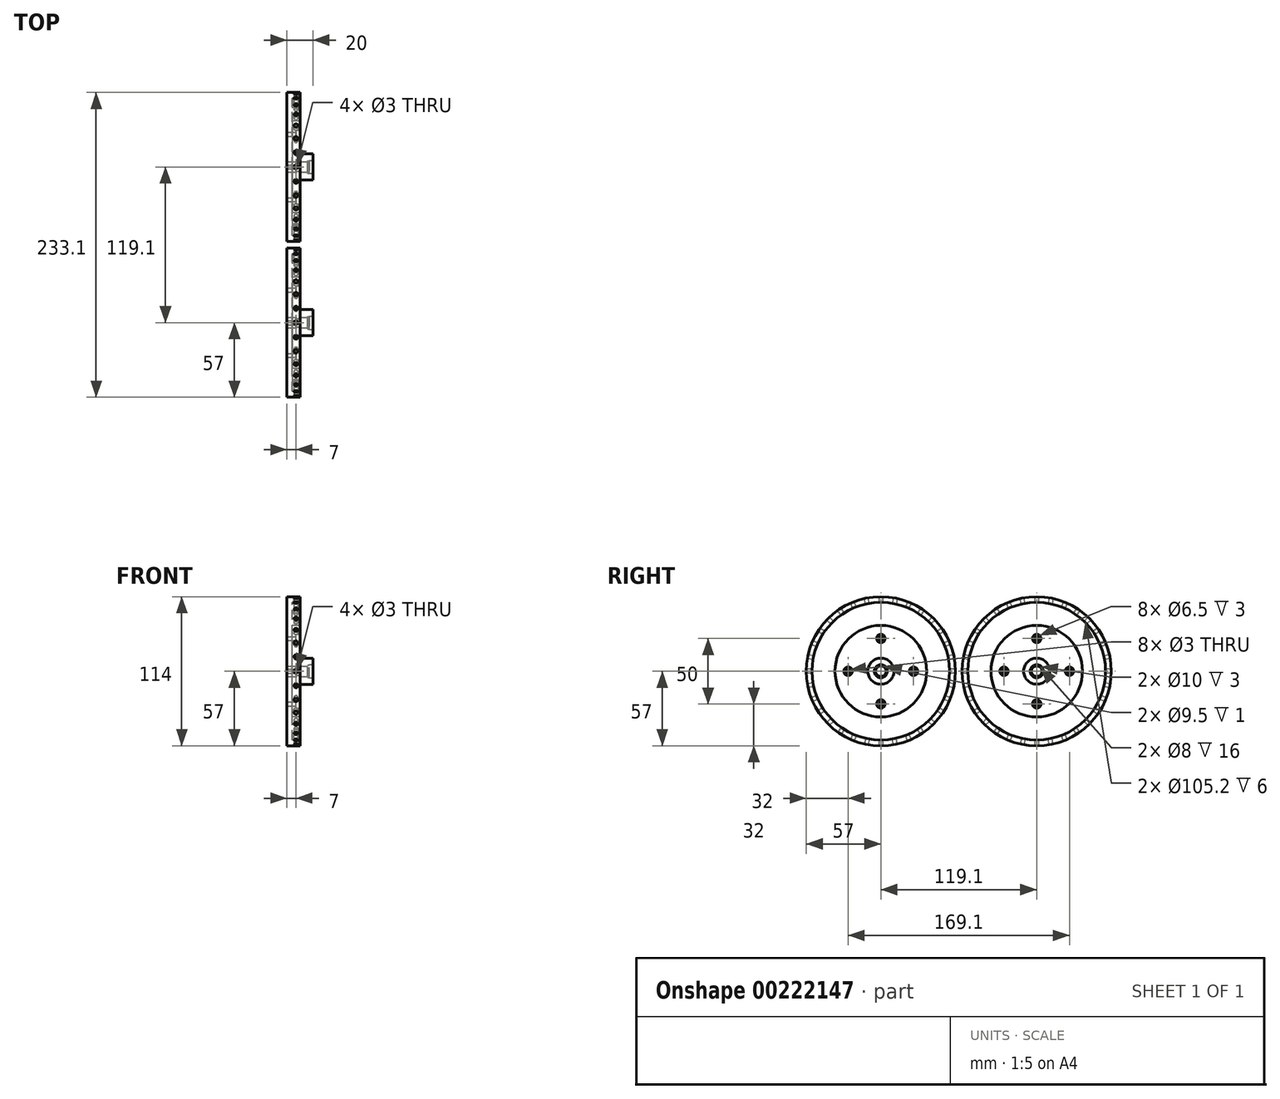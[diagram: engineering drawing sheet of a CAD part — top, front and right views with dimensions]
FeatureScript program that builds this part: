
annotation { "Feature Type Name" : "Feature", "Feature Type Description" : "" }
export const myFeature = defineFeature(function(context is Context, id is Id, definition is map)
    precondition{}
    {
        {
            var Q0;
            Q0=qCreatedBy(makeId("Right.planeOp"),FACE);
            var sketch = newSketch(context, id + "F0", { "sketchPlane" : qUnion([Q0])});
            skCircle(sketch, "E0", {"center": v(0, 0) * mm, "radius": 57 * mm});
            skCircle(sketch, "E1", {"center": v(0, 0) * mm, "radius": 52.6 * mm});
            skSolve(sketch);
        }
        {
            var Q0;
            Q0=qSketchRegion(id+"F0",true);
            extrude(context, id + "F1", {"entities" : qUnion([Q0]), "endBound" : BoundingType.SYMMETRIC, "depth" : 20 * mm});
        }
        {
            var Q0;
            Q0=qCreatedBy(makeId("Right.planeOp"),FACE);
            var sketch = newSketch(context, id + "F2", { "sketchPlane" : qUnion([Q0])});
            skCircle(sketch, "E2", {"center": v(0, 0) * mm, "radius": 52.6 * mm});
            skCircle(sketch, "E3", {"center": v(0, 0) * mm, "radius": 4 * mm});
            skSolve(sketch);
        }
        {
            var Q0;
            Q0=qSketchRegion(id+"F2",true);
            extrude(context, id + "F3", {"entities" : qUnion([Q0]), "operationType" : NewBodyOperationType.ADD, "endBound" : BoundingType.SYMMETRIC, "depth" : 8 * mm});
        }
        {
            var Q0;
            Q0=qCreatedBy(makeId("Top.planeOp"),FACE);
            var sketch = newSketch(context, id + "F4", { "sketchPlane" : qUnion([Q0])});
            skCircle(sketch, "E4", {"center": v(0, 0) * mm, "radius": 7 * mm, "construction": true});
            skCircle(sketch, "E5", {"center": v(-7, 0) * mm, "radius": 1.5 * mm});
            skCircle(sketch, "E6", {"center": v(7, 0) * mm, "radius": 1.5 * mm});
            skSolve(sketch);
        }
        {
            var Q0;
            Q0=qSketchRegion(id+"F4",true);
            extrude(context, id + "F5", {"entities" : qUnion([Q0]), "endBound" : BoundingType.SYMMETRIC, "depth" : 160 * mm, "hasSecondDirection" : true, "secondDirectionBound" : SecondDirectionBoundingType.THROUGH_ALL, "secondDirectionOppositeDirection" : true, "secondDirectionDepth" : 25 * mm});
        }
        {
            var Q0;
            Q0=qCreatedBy(makeId("Front.planeOp"),FACE);
            var sketch = newSketch(context, id + "F6", { "sketchPlane" : qUnion([Q0])});
            skLineSegment(sketch, "E7", {"start": v(28.93, 0) * mm, "end": v(-37.29, 0) * mm, "construction": true});
            skSolve(sketch);
        }
        {
            var Q0;
            Q0=makeQuery(id+"F5.opExtrude","SWEPT_BODY",BODY,{"disambiguationData":[OSD([sQuery(id+"F4.wireOp",EDGE,"E6")])]});
            var Q1;
            Q1=makeQuery(id+"F5.opExtrude","SWEPT_BODY",BODY,{"disambiguationData":[OSD([sQuery(id+"F4.wireOp",EDGE,"E5")])]});
            var Q2;
            Q2=sQuery(id+"F6.wireOp",EDGE,"E7");
            circularPattern(context, id + "F7", {"operationType" : NewBodyOperationType.REMOVE, "entities" : qUnion([Q0, Q1]), "axis" : qUnion([Q2]), "angle" : 180 * degree, "instanceCount" : 17, "equalSpace" : true});
        }
        {
            var Q0;
            Q0=qCreatedBy(makeId("Right.planeOp"),FACE);
            var sketch = newSketch(context, id + "F8", { "sketchPlane" : qUnion([Q0])});
            skCircle(sketch, "E8", {"center": v(0, 0) * mm, "radius": 10 * mm});
            skSolve(sketch);
        }
        {
            var Q0;
            Q0=qSketchRegion(id+"F8",true);
            extrude(context, id + "F9", {"entities" : qUnion([Q0]), "operationType" : NewBodyOperationType.ADD, "endBound" : BoundingType.SYMMETRIC, "depth" : 40 * mm});
        }
        {
            var Q0;
            Q0=makeQuery(id+"F9.opExtrude","CAP_FACE",FACE,{"disambiguationData":[OSD([sQuery(id+"F8.wireOp",EDGE,"E8")])],"isStart":false});
            var sketch = newSketch(context, id + "F10", { "sketchPlane" : qUnion([Q0])});
            skCircle(sketch, "E9", {"center": v(0, 0) * mm, "radius": 5 * mm});
            skSolve(sketch);
        }
        {
            var Q0;
            Q0=qSketchRegion(id+"F10",true);
            extrude(context, id + "F11", {"entities" : qUnion([Q0]), "operationType" : NewBodyOperationType.REMOVE, "oppositeDirection" : true, "depth" : 3 * mm});
        }
        {
            var Q0;
            Q0=makeQuery(id+"F9.opExtrude","CAP_FACE",FACE,{"disambiguationData":[OSD([sQuery(id+"F8.wireOp",EDGE,"E8")])],"isStart":true});
            var sketch = newSketch(context, id + "F12", { "sketchPlane" : qUnion([Q0])});
            skCircle(sketch, "E10", {"center": v(0, 0) * mm, "radius": 5 * mm});
            skSolve(sketch);
        }
        {
            var Q0;
            Q0=qSketchRegion(id+"F12",true);
            extrude(context, id + "F13", {"entities" : qUnion([Q0]), "operationType" : NewBodyOperationType.REMOVE, "oppositeDirection" : true, "depth" : 3 * mm});
        }
        {
            var Q0;
            Q0=makeQuery(id+"F11.boolean.opBoolean","COPY",FACE,{"derivedFrom":makeQuery(id+"F11.opExtrude","CAP_FACE",FACE,{"disambiguationData":[OSD([sQuery(id+"F10.wireOp",EDGE,"E9")])],"isStart":false})});
            var sketch = newSketch(context, id + "F14", { "sketchPlane" : qUnion([Q0])});
            skCircle(sketch, "E11", {"center": v(0, 0) * mm, "radius": 4.75 * mm});
            skSolve(sketch);
        }
        {
            var Q0;
            Q0=qSketchRegion(id+"F14",true);
            extrude(context, id + "F15", {"entities" : qUnion([Q0]), "operationType" : NewBodyOperationType.REMOVE, "oppositeDirection" : true, "depth" : 1 * mm});
        }
        {
            var Q0;
            Q0=makeQuery(id+"F13.boolean.opBoolean","COPY",FACE,{"derivedFrom":makeQuery(id+"F13.opExtrude","CAP_FACE",FACE,{"disambiguationData":[OSD([sQuery(id+"F12.wireOp",EDGE,"E10")])],"isStart":false})});
            var sketch = newSketch(context, id + "F16", { "sketchPlane" : qUnion([Q0])});
            skCircle(sketch, "E12", {"center": v(0, 0) * mm, "radius": 4.75 * mm});
            skSolve(sketch);
        }
        {
            var Q0;
            Q0=qSketchRegion(id+"F16",true);
            extrude(context, id + "F17", {"entities" : qUnion([Q0]), "operationType" : NewBodyOperationType.REMOVE, "oppositeDirection" : true, "depth" : 1 * mm});
        }
        {
            var Q0;
            Q0=makeQuery(id+"F9.opExtrude","CAP_FACE",FACE,{"disambiguationData":[OSD([sQuery(id+"F8.wireOp",EDGE,"E8")])],"isStart":false});
            var sketch = newSketch(context, id + "F18", { "sketchPlane" : qUnion([Q0])});
            skCircle(sketch, "E13", {"center": v(0, 0) * mm, "radius": 4 * mm});
            skSolve(sketch);
        }
        {
            var Q0;
            Q0=qSketchRegion(id+"F18",true);
            extrude(context, id + "F19", {"entities" : qUnion([Q0]), "operationType" : NewBodyOperationType.REMOVE, "endBound" : BoundingType.THROUGH_ALL, "oppositeDirection" : true, "depth" : 25 * mm});
        }
        {
            var Q0;
            Q0=qCreatedBy(makeId("Front.planeOp"),FACE);
            var sketch = newSketch(context, id + "F20", { "sketchPlane" : qUnion([Q0])});
            skCircle(sketch, "E14", {"center": v(0, 0) * mm, "radius": 17 * mm, "construction": true});
            skLineSegment(sketch, "E15", {"start": v(-17, 0) * mm, "end": v(-17, 16.39) * mm, "construction": true});
            skCircle(sketch, "E16", {"center": v(-17, 0) * mm, "radius": 10 * mm, "construction": true});
            skCircle(sketch, "E17", {"center": v(-17, 0) * mm, "radius": 8.5 * mm, "construction": true});
            skLineSegment(sketch, "E18", {"start": v(-17, 10) * mm, "end": v(-16, 10) * mm});
            skLineSegment(sketch, "E19", {"start": v(-16, 10) * mm, "end": v(-17, 8.5) * mm});
            skLineSegment(sketch, "E20.MirrorCS", {"start": v(-17, 10) * mm, "end": v(-18, 10) * mm});
            skLineSegment(sketch, "E21.MirrorCS", {"start": v(-18, 10) * mm, "end": v(-17, 8.5) * mm});
            skSolve(sketch);
        }
        {
            var Q0;
            Q0=qCreatedBy(makeId("Front.planeOp"),FACE);
            var sketch = newSketch(context, id + "F21", { "sketchPlane" : qUnion([Q0])});
            skLineSegment(sketch, "E22", {"start": v(-63.54, 0) * mm, "end": v(70.4, 0) * mm, "construction": true});
            skSolve(sketch);
        }
        {
            var Q0;
            Q0=qSketchRegion(id+"F20",true);
            var Q1;
            Q1=sQuery(id+"F21.wireOp",EDGE,"E22");
            revolve(context, id + "F22", {"operationType" : NewBodyOperationType.REMOVE, "entities" : qUnion([Q0]), "axis" : qUnion([Q1]), "revolveType" : RevolveType.FULL, "oppositeDirection" : true});
        }
        {
            var Q0;
            Q0=qCreatedBy(makeId("Right.planeOp"),FACE);
            var sketch = newSketch(context, id + "F23", { "sketchPlane" : qUnion([Q0])});
            skCircle(sketch, "E23", {"center": v(0, 0) * mm, "radius": 4 * mm});
            skCircle(sketch, "E24", {"center": v(0, 0) * mm, "radius": 35 * mm});
            skSolve(sketch);
        }
        {
            var Q0;
            Q0=qSketchRegion(id+"F23",true);
            extrude(context, id + "F24", {"entities" : qUnion([Q0]), "operationType" : NewBodyOperationType.ADD, "endBound" : BoundingType.SYMMETRIC, "depth" : 20 * mm});
        }
        {
            var Q0;
            Q0=makeQuery(id+"F24.opExtrude","CAP_FACE",FACE,{"disambiguationData":[OSD([sQuery(id+"F23.wireOp",EDGE,"E23"),sQuery(id+"F23.wireOp",EDGE,"E24")])],"isStart":false});
            var sketch = newSketch(context, id + "F25", { "sketchPlane" : qUnion([Q0])});
            skCircle(sketch, "E25", {"center": v(0, 0) * mm, "radius": 25 * mm, "construction": true});
            skCircle(sketch, "E26", {"center": v(-25, 0) * mm, "radius": 3.25 * mm});
            skCircle(sketch, "E27.1.0", {"center": v(0, 25) * mm, "radius": 3.25 * mm});
            skCircle(sketch, "E27.2.0", {"center": v(25, 0) * mm, "radius": 3.25 * mm});
            skCircle(sketch, "E27.3.0", {"center": v(0, -25) * mm, "radius": 3.25 * mm});
            skLineSegment(sketch, "E27.anchor1", {"start": v(0, 0) * mm, "end": v(-25, 0) * mm, "construction": true});
            skLineSegment(sketch, "E27.anchor2", {"start": v(0, 0) * mm, "end": v(0, -25) * mm, "construction": true});
            skSolve(sketch);
        }
        {
            var Q0;
            Q0 = qSketchRegion(id + "F25", true);
            extrude(context, id + "F26", {"entities" : qUnion([Q0]), "operationType" : NewBodyOperationType.REMOVE, "oppositeDirection" : true, "depth" : 3 * mm});
        }
        {
            var Q0;
            Q0=makeQuery(id+"F24.opExtrude","CAP_FACE",FACE,{"disambiguationData":[OSD([sQuery(id+"F23.wireOp",EDGE,"E23"),sQuery(id+"F23.wireOp",EDGE,"E24")])],"isStart":false});
            var sketch = newSketch(context, id + "F27", { "sketchPlane" : qUnion([Q0])});
            skCircle(sketch, "E28", {"center": v(-25, 0) * mm, "radius": 1.5 * mm});
            skCircle(sketch, "E29.1.0", {"center": v(0, -25) * mm, "radius": 1.5 * mm});
            skCircle(sketch, "E29.2.0", {"center": v(25, 0) * mm, "radius": 1.5 * mm});
            skCircle(sketch, "E29.3.0", {"center": v(0, 25) * mm, "radius": 1.5 * mm});
            skPoint(sketch, "E29.center", {"position": v(0, 0) * mm});
            skSolve(sketch);
        }
        {
            var Q0;
            Q0 = qSketchRegion(id + "F27", true);
            extrude(context, id + "F28", {"entities" : qUnion([Q0]), "operationType" : NewBodyOperationType.REMOVE, "endBound" : BoundingType.THROUGH_ALL, "oppositeDirection" : true, "depth" : 25 * mm});
        }
        {
            var Q0;
            Q0=qCreatedBy(makeId("Right.planeOp"),FACE);
            var sketch = newSketch(context, id + "F29", { "sketchPlane" : qUnion([Q0])});
            skLineSegment(sketch, "E30.bottom", {"start": v(-66.66, 64.91) * mm, "end": v(66.47, 64.91) * mm});
            skLineSegment(sketch, "E30.top", {"start": v(-66.66, -67.05) * mm, "end": v(66.47, -67.05) * mm});
            skLineSegment(sketch, "E30.left", {"start": v(-66.66, 64.91) * mm, "end": v(-66.66, -67.05) * mm});
            skLineSegment(sketch, "E30.right", {"start": v(66.47, 64.91) * mm, "end": v(66.47, -67.05) * mm});
            skSolve(sketch);
        }
        {
            var Q0;
            Q0=makeQuery(id+"F29.imprint","IMPRINT",FACE,{"disambiguationData":[TD([[makeQuery(id+"F29.imprint","IMPRINT",EDGE,{"derivedFrom":sQuery(id+"F29.wireOp",EDGE,"E30.bottom")}),-1.0]])]});
            extrude(context, id + "F30", {"entities" : qUnion([Q0]), "operationType" : NewBodyOperationType.REMOVE, "endBound" : BoundingType.THROUGH_ALL, "oppositeDirection" : true, "depth" : 25 * mm});
        }
        {
            var Q0;
            Q0=makeQuery(id+"F1.opExtrude","SWEPT_BODY",BODY,{"disambiguationData":[OSD([sQuery(id+"F0.wireOp",EDGE,"E0"),sQuery(id+"F0.wireOp",EDGE,"E1")])]});
            transform(context, id + "F31", {"entities" : qUnion([Q0]), "transformType" : TransformType.TRANSLATION_3D, "dx" : 0 * mm, "dy" : 119.1 * mm, "dz" : 0 * mm, "makeCopy" : true});
        }
    });
